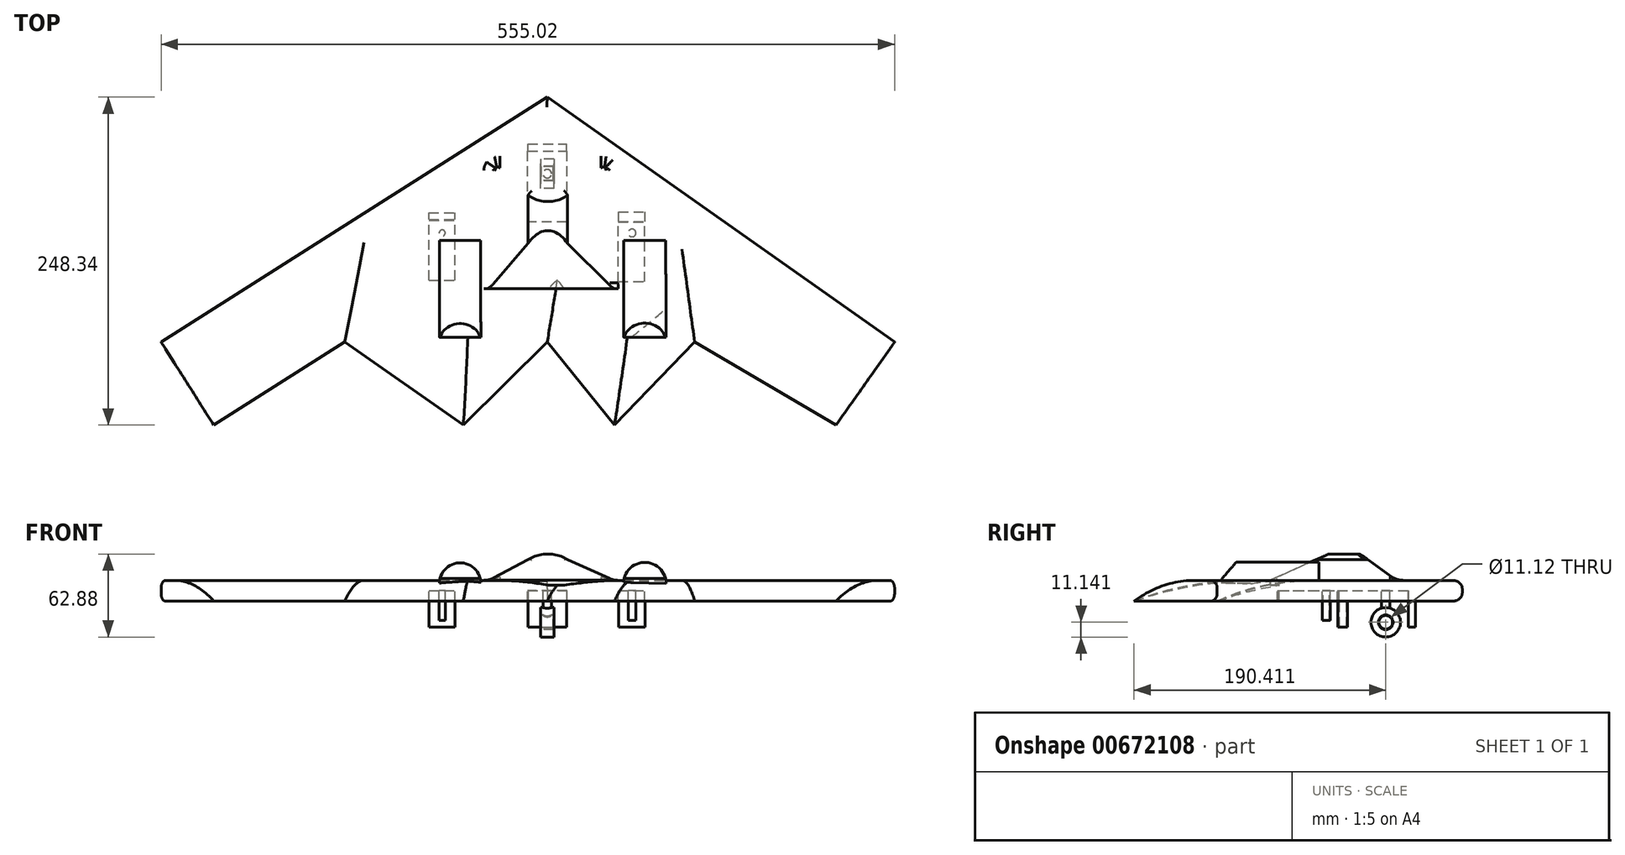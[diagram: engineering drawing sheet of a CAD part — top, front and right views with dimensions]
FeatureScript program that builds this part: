
annotation { "Feature Type Name" : "Feature", "Feature Type Description" : "" }
export const myFeature = defineFeature(function(context is Context, id is Id, definition is map)
    precondition{}
    {
        {
            var Q0;
            Q0=qCreatedBy(makeId("Top.planeOp"),FACE);
            var sketch = newSketch(context, id + "F0", { "sketchPlane" : qUnion([Q0])});
            skLineSegment(sketch, "E0", {"start": v(-292.15, -40.35) * mm, "end": v(0, 145.12) * mm});
            skLineSegment(sketch, "E1", {"start": v(0, 145.12) * mm, "end": v(262.87, -40.35) * mm});
            skLineSegment(sketch, "E2", {"start": v(262.87, -40.35) * mm, "end": v(218.51, -103.22) * mm});
            skLineSegment(sketch, "E3", {"start": v(-292.15, -40.35) * mm, "end": v(-252.24, -103.22) * mm});
            skLineSegment(sketch, "E4", {"start": v(-252.24, -103.22) * mm, "end": v(-153.22, -40.35) * mm});
            skLineSegment(sketch, "E5", {"start": v(-153.22, -40.35) * mm, "end": v(-63.45, -103.22) * mm});
            skLineSegment(sketch, "E6", {"start": v(218.51, -103.22) * mm, "end": v(111.56, -40.35) * mm});
            skLineSegment(sketch, "E7", {"start": v(111.56, -40.35) * mm, "end": v(50.9, -103.22) * mm});
            skLineSegment(sketch, "E8", {"start": v(50.9, -103.22) * mm, "end": v(0, -40.35) * mm});
            skLineSegment(sketch, "E9", {"start": v(0, -40.35) * mm, "end": v(-63.45, -103.22) * mm});
            skSolve(sketch);
        }
        {
            var Q0;
            Q0 = qSketchRegion(id + "F0", true);
            extrude(context, id + "F1", {"entities" : qUnion([Q0]), "endBound" : BoundingType.SYMMETRIC, "depth" : 15.75 * mm, "offsetDistance" : 25.4 * mm});
        }
        {
            var Q0;
            Q0=makeQuery(id+"F1.opExtrude","CAP_EDGE",EDGE,{"disambiguationData":[OSD([sQuery(id+"F0.wireOp",EDGE,"E1")])],"isStart":true});
            var Q1;
            Q1=makeQuery(id+"F1.opExtrude","CAP_EDGE",EDGE,{"disambiguationData":[OSD([sQuery(id+"F0.wireOp",EDGE,"E1")])],"isStart":false});
            var Q2;
            Q2=makeQuery(id+"F1.opExtrude","CAP_EDGE",EDGE,{"disambiguationData":[OSD([sQuery(id+"F0.wireOp",EDGE,"E0")])],"isStart":false});
            var Q3;
            Q3=makeQuery(id+"F1.opExtrude","CAP_EDGE",EDGE,{"disambiguationData":[OSD([sQuery(id+"F0.wireOp",EDGE,"E0")])],"isStart":true});
            fillet(context, id + "F2", {"entities" : qUnion([Q0, Q1, Q2, Q3]), "radius" : 6.13 * mm, "tangentPropagation" : true, "allowEdgeOverflow" : false});
        }
        {
            var Q0;
            Q0=makeQuery(id+"F1.opExtrude","CAP_EDGE",EDGE,{"disambiguationData":[OSD([sQuery(id+"F0.wireOp",EDGE,"E6")])],"isStart":false});
            var Q1;
            Q1=makeQuery(id+"F1.opExtrude","CAP_EDGE",EDGE,{"disambiguationData":[OSD([sQuery(id+"F0.wireOp",EDGE,"E7")])],"isStart":false});
            var Q2;
            Q2=makeQuery(id+"F1.opExtrude","CAP_EDGE",EDGE,{"disambiguationData":[OSD([sQuery(id+"F0.wireOp",EDGE,"E9")])],"isStart":false});
            var Q3;
            Q3=makeQuery(id+"F1.opExtrude","CAP_EDGE",EDGE,{"disambiguationData":[OSD([sQuery(id+"F0.wireOp",EDGE,"E4")])],"isStart":false});
            fillet(context, id + "F3", {"entities" : qUnion([Q0, Q1, Q2, Q3]), "radius" : 106.7 * mm, "tangentPropagation" : true, "allowEdgeOverflow" : false});
        }
        {
            var Q0;
            Q0=makeQuery(id+"F1.opExtrude","CAP_EDGE",EDGE,{"disambiguationData":[OSD([sQuery(id+"F0.wireOp",EDGE,"E5")])],"isStart":false});
            var Q1;
            Q1=makeQuery(id+"F1.opExtrude","CAP_EDGE",EDGE,{"disambiguationData":[OSD([sQuery(id+"F0.wireOp",EDGE,"E8")])],"isStart":false});
            fillet(context, id + "F4", {"entities" : qUnion([Q0, Q1]), "radius" : 163.11 * mm, "tangentPropagation" : true, "allowEdgeOverflow" : false});
        }
        {
            var Q0;
            Q0=qCreatedBy(makeId("Front.planeOp"),FACE);
            var sketch = newSketch(context, id + "F5", { "sketchPlane" : qUnion([Q0])});
            skArc(sketch, "E10", {"start": v(15.33, 23.56) * mm, "mid": v(0.48, 27.88) * mm, "end": v(-14.38, 23.56) * mm});
            skLineSegment(sketch, "E11", {"start": v(15.33, 23.56) * mm, "end": v(58.69, 4.08) * mm});
            skLineSegment(sketch, "E12", {"start": v(-14.38, 23.56) * mm, "end": v(-50.75, 4.4) * mm});
            skLineSegment(sketch, "E13", {"start": v(-50.75, 6.02) * mm, "end": v(-50.75, 4.4) * mm});
            skLineSegment(sketch, "E14", {"start": v(-50.75, 4.4) * mm, "end": v(58.69, 4.08) * mm});
            skSolve(sketch);
        }
        {
            var Q0;
            Q0 = qSketchRegion(id + "F5", true);
            extrude(context, id + "F6", {"entities" : qUnion([Q0]), "operationType" : NewBodyOperationType.ADD, "oppositeDirection" : true, "depth" : 94.74 * mm, "offsetDistance" : 25.4 * mm});
        }
        {
            var Q0;
            Q0=qCreatedBy(makeId("Right.planeOp"),FACE);
            var sketch = newSketch(context, id + "F7", { "sketchPlane" : qUnion([Q0])});
            skLineSegment(sketch, "E15", {"start": v(60.3, 33.11) * mm, "end": v(94.75, 8.43) * mm});
            skLineSegment(sketch, "E16", {"start": v(94.75, 8.43) * mm, "end": v(114.8, 41.67) * mm});
            skLineSegment(sketch, "E17", {"start": v(114.8, 41.67) * mm, "end": v(60.3, 33.11) * mm});
            skSolve(sketch);
        }
        {
            var Q0;
            Q0 = qSketchRegion(id + "F7", true);
            extrude(context, id + "F8", {"entities" : qUnion([Q0]), "operationType" : NewBodyOperationType.REMOVE, "endBound" : BoundingType.SYMMETRIC, "oppositeDirection" : true, "depth" : 1325.88 * mm, "offsetDistance" : 25.4 * mm});
        }
        {
            var Q0;
            Q0=makeQuery(id+"F8.boolean.opBoolean","INTERSECT",EDGE,{"derivedFrom":[makeQuery(id+"F6.opExtrude","CAP_FACE",FACE,{"disambiguationData":[OSD([sQuery(id+"F5.wireOp",EDGE,"E10"),sQuery(id+"F5.wireOp",EDGE,"E11"),sQuery(id+"F5.wireOp",EDGE,"E12"),sQuery(id+"F5.wireOp",EDGE,"E14")])],"isStart":false}),makeQuery(id+"F8.opExtrude","SWEPT_FACE",FACE,{"disambiguationData":[OSD([sQuery(id+"F7.wireOp",EDGE,"E15")])]})]});
            fillet(context, id + "F9", {"entities" : qUnion([Q0]), "radius" : 0.08 * mm, "tangentPropagation" : true, "allowEdgeOverflow" : false});
        }
        {
            var Q0;
            Q0=makeQuery(id+"F8.boolean.opBoolean","INTERSECT",EDGE,{"derivedFrom":[makeQuery(id+"F6.opExtrude","SWEPT_FACE",FACE,{"disambiguationData":[OSD([sQuery(id+"F5.wireOp",EDGE,"E11")])]}),makeQuery(id+"F8.opExtrude","SWEPT_FACE",FACE,{"disambiguationData":[OSD([sQuery(id+"F7.wireOp",EDGE,"E15")])]})]});
            var Q1;
            Q1=makeQuery(id+"F8.boolean.opBoolean","INTERSECT",EDGE,{"derivedFrom":[makeQuery(id+"F6.opExtrude","SWEPT_FACE",FACE,{"disambiguationData":[OSD([sQuery(id+"F5.wireOp",EDGE,"E10")])]}),makeQuery(id+"F8.opExtrude","SWEPT_FACE",FACE,{"disambiguationData":[OSD([sQuery(id+"F7.wireOp",EDGE,"E15")])]})]});
            var Q2;
            Q2=makeQuery(id+"F8.boolean.opBoolean","INTERSECT",EDGE,{"derivedFrom":[makeQuery(id+"F6.opExtrude","SWEPT_FACE",FACE,{"disambiguationData":[OSD([sQuery(id+"F5.wireOp",EDGE,"E12")])]}),makeQuery(id+"F8.opExtrude","SWEPT_FACE",FACE,{"disambiguationData":[OSD([sQuery(id+"F7.wireOp",EDGE,"E15")])]})]});
            fillet(context, id + "F10", {"entities" : qUnion([Q0, Q1, Q2]), "radius" : 5.08 * mm, "tangentPropagation" : true, "allowEdgeOverflow" : false});
        }
        {
            var Q0;
            Q0=qCreatedBy(makeId("Right.planeOp"),FACE);
            var sketch = newSketch(context, id + "F11", { "sketchPlane" : qUnion([Q0])});
            skLineSegment(sketch, "E18", {"start": v(0, 7.99) * mm, "end": v(46.44, 28.93) * mm});
            skLineSegment(sketch, "E19", {"start": v(46.44, 28.93) * mm, "end": v(-11.72, 36.75) * mm});
            skLineSegment(sketch, "E20", {"start": v(-11.72, 36.75) * mm, "end": v(0, 7.99) * mm});
            skSolve(sketch);
        }
        {
            var Q0;
            Q0 = qSketchRegion(id + "F11", true);
            extrude(context, id + "F12", {"entities" : qUnion([Q0]), "operationType" : NewBodyOperationType.REMOVE, "endBound" : BoundingType.SYMMETRIC, "oppositeDirection" : true, "depth" : 115.32 * mm, "offsetDistance" : 25.4 * mm});
        }
        {
            var Q0;
            Q0=qCreatedBy(makeId("Front.planeOp"),FACE);
            var sketch = newSketch(context, id + "F13", { "sketchPlane" : qUnion([Q0])});
            skArc(sketch, "E21", {"start": v(89.94, 5.45) * mm, "mid": v(74.32, 21.57) * mm, "end": v(57.8, 6.37) * mm});
            skArc(sketch, "E22", {"start": v(-50.13, 6.14) * mm, "mid": v(-66.32, 21.19) * mm, "end": v(-81.6, 5.22) * mm});
            skLineSegment(sketch, "E23", {"start": v(89.94, 5.45) * mm, "end": v(57.8, 6.37) * mm});
            skLineSegment(sketch, "E24", {"start": v(-50.13, 6.14) * mm, "end": v(-81.6, 5.22) * mm});
            skSolve(sketch);
        }
        {
            var Q0;
            Q0 = qSketchRegion(id + "F13", true);
            extrude(context, id + "F14", {"entities" : qUnion([Q0]), "operationType" : NewBodyOperationType.ADD, "endBound" : BoundingType.SYMMETRIC, "oppositeDirection" : true, "depth" : 73.15 * mm, "offsetDistance" : 25.4 * mm});
        }
        {
            var Q0;
            Q0=qCreatedBy(makeId("Right.planeOp"),FACE);
            var sketch = newSketch(context, id + "F15", { "sketchPlane" : qUnion([Q0])});
            skLineSegment(sketch, "E25", {"start": v(-36.97, 8.92) * mm, "end": v(-22.55, 25.54) * mm});
            skLineSegment(sketch, "E26", {"start": v(-22.55, 25.54) * mm, "end": v(-55.3, 20.9) * mm});
            skLineSegment(sketch, "E27", {"start": v(-55.3, 20.9) * mm, "end": v(-36.97, 8.92) * mm});
            skSolve(sketch);
        }
        {
            var Q0;
            Q0 = qSketchRegion(id + "F15", true);
            extrude(context, id + "F16", {"entities" : qUnion([Q0]), "operationType" : NewBodyOperationType.REMOVE, "endBound" : BoundingType.SYMMETRIC, "oppositeDirection" : true, "depth" : 313.94 * mm, "offsetDistance" : 25.4 * mm});
        }
        {
            var Q0;
            {var subQ0=makeQuery(id+"F6.opExtrude","CAP_FACE",FACE,{"disambiguationData":[OSD([sQuery(id+"F5.wireOp",EDGE,"E10"),sQuery(id+"F5.wireOp",EDGE,"E11"),sQuery(id+"F5.wireOp",EDGE,"E12"),sQuery(id+"F5.wireOp",EDGE,"E14")])],"isStart":false});Q0=makeQuery(id+"F9.opFillet","BLEND_EDGE",EDGE,{"blendedFrom":[makeQuery(id+"F8.boolean.opBoolean","INTERSECT",EDGE,{"derivedFrom":[subQ0,makeQuery(id+"F8.opExtrude","SWEPT_FACE",FACE,{"disambiguationData":[OSD([sQuery(id+"F7.wireOp",EDGE,"E15")])]})]}),subQ0],"blendedInto":[subQ0]});}
            var Q1;
            Q1=makeQuery(id+"F6.boolean.opBoolean","INTERSECT",EDGE,{"derivedFrom":[makeQuery(id+"F1.opExtrude","CAP_FACE",FACE,{"disambiguationData":[OSD([sQuery(id+"F0.wireOp",EDGE,"E0"),sQuery(id+"F0.wireOp",EDGE,"E1"),sQuery(id+"F0.wireOp",EDGE,"E2"),sQuery(id+"F0.wireOp",EDGE,"E3"),sQuery(id+"F0.wireOp",EDGE,"E4"),sQuery(id+"F0.wireOp",EDGE,"E5"),sQuery(id+"F0.wireOp",EDGE,"E6"),sQuery(id+"F0.wireOp",EDGE,"E7"),sQuery(id+"F0.wireOp",EDGE,"E8"),sQuery(id+"F0.wireOp",EDGE,"E9")])],"isStart":false}),makeQuery(id+"F6.opExtrude","CAP_FACE",FACE,{"disambiguationData":[OSD([sQuery(id+"F5.wireOp",EDGE,"E10"),sQuery(id+"F5.wireOp",EDGE,"E11"),sQuery(id+"F5.wireOp",EDGE,"E12"),sQuery(id+"F5.wireOp",EDGE,"E14")])],"isStart":false})]});
            fillet(context, id + "F17", {"entities" : qUnion([Q0, Q1]), "radius" : 15.33 * mm, "tangentPropagation" : true, "allowEdgeOverflow" : false});
        }
        {
            var Q0;
            Q0=qCreatedBy(makeId("Top.planeOp"),FACE);
            var sketch = newSketch(context, id + "F18", { "sketchPlane" : qUnion([Q0])});
            skLineSegment(sketch, "E28.bottom", {"start": v(14.85, 50.72) * mm, "end": v(-14.85, 50.72) * mm});
            skLineSegment(sketch, "E28.top", {"start": v(14.85, 104.24) * mm, "end": v(-14.85, 104.24) * mm});
            skLineSegment(sketch, "E28.left", {"start": v(14.85, 50.72) * mm, "end": v(14.85, 104.24) * mm});
            skLineSegment(sketch, "E28.right", {"start": v(-14.85, 50.72) * mm, "end": v(-14.85, 104.24) * mm});
            skPoint(sketch, "E28.middle", {"position": v(0, 77.48) * mm});
            skLineSegment(sketch, "E29.bottom", {"start": v(-89.47, 6.48) * mm, "end": v(-69.8, 6.48) * mm});
            skLineSegment(sketch, "E29.top", {"start": v(-89.47, 51.8) * mm, "end": v(-69.8, 51.8) * mm});
            skLineSegment(sketch, "E29.left", {"start": v(-89.47, 6.48) * mm, "end": v(-89.47, 51.8) * mm});
            skLineSegment(sketch, "E29.right", {"start": v(-69.8, 6.48) * mm, "end": v(-69.8, 51.8) * mm});
            skLineSegment(sketch, "E30.bottom", {"start": v(53.63, 5.38) * mm, "end": v(73.84, 5.38) * mm});
            skLineSegment(sketch, "E30.top", {"start": v(53.63, 50.72) * mm, "end": v(73.84, 50.72) * mm});
            skLineSegment(sketch, "E30.left", {"start": v(53.63, 5.38) * mm, "end": v(53.63, 50.72) * mm});
            skLineSegment(sketch, "E30.right", {"start": v(73.84, 5.38) * mm, "end": v(73.84, 50.72) * mm});
            skSolve(sketch);
        }
        {
            var Q0;
            Q0 = qSketchRegion(id + "F18", true);
            extrude(context, id + "F19", {"entities" : qUnion([Q0]), "operationType" : NewBodyOperationType.REMOVE, "oppositeDirection" : true, "depth" : 25.4 * mm, "offsetDistance" : 25.4 * mm});
        }
        {
            var Q0;
            Q0=qCreatedBy(makeId("Top.planeOp"),FACE);
            var sketch = newSketch(context, id + "F20", { "sketchPlane" : qUnion([Q0])});
            skLineSegment(sketch, "E31.bottom", {"start": v(-14.6, 104.17) * mm, "end": v(14.79, 104.17) * mm});
            skLineSegment(sketch, "E31.top", {"start": v(-14.6, 109.53) * mm, "end": v(14.79, 109.53) * mm});
            skLineSegment(sketch, "E31.left", {"start": v(-14.6, 104.17) * mm, "end": v(-14.6, 109.53) * mm});
            skLineSegment(sketch, "E31.right", {"start": v(14.79, 104.17) * mm, "end": v(14.79, 109.53) * mm});
            skLineSegment(sketch, "E32.bottom", {"start": v(53.92, 51.04) * mm, "end": v(74.06, 51.04) * mm});
            skLineSegment(sketch, "E32.top", {"start": v(53.92, 58.19) * mm, "end": v(74.06, 58.19) * mm});
            skLineSegment(sketch, "E32.left", {"start": v(53.92, 51.04) * mm, "end": v(53.92, 58.19) * mm});
            skLineSegment(sketch, "E32.right", {"start": v(74.06, 51.04) * mm, "end": v(74.06, 58.19) * mm});
            skLineSegment(sketch, "E33.bottom", {"start": v(-89.62, 52.34) * mm, "end": v(-69.81, 52.34) * mm});
            skLineSegment(sketch, "E33.top", {"start": v(-89.62, 57.54) * mm, "end": v(-69.81, 57.54) * mm});
            skLineSegment(sketch, "E33.left", {"start": v(-89.62, 52.34) * mm, "end": v(-89.62, 57.54) * mm});
            skLineSegment(sketch, "E33.right", {"start": v(-69.81, 52.34) * mm, "end": v(-69.81, 57.54) * mm});
            skSolve(sketch);
        }
        {
            var Q0;
            Q0 = qSketchRegion(id + "F20", true);
            extrude(context, id + "F21", {"entities" : qUnion([Q0]), "operationType" : NewBodyOperationType.ADD, "oppositeDirection" : true, "depth" : 27.43 * mm, "offsetDistance" : 25.4 * mm});
        }
        {
            var Q0;
            Q0=qCreatedBy(makeId("Top.planeOp"),FACE);
            var sketch = newSketch(context, id + "F22", { "sketchPlane" : qUnion([Q0])});
            skCircle(sketch, "E34", {"center": v(0, 87.15) * mm, "radius": 3.23 * mm});
            skSolve(sketch);
        }
        {
            var Q0;
            Q0 = qSketchRegion(id + "F22", true);
            extrude(context, id + "F23", {"entities" : qUnion([Q0]), "operationType" : NewBodyOperationType.ADD, "oppositeDirection" : true, "depth" : 20.83 * mm, "offsetDistance" : 25.4 * mm});
        }
        {
            var Q0;
            Q0=qCreatedBy(makeId("Right.planeOp"),FACE);
            var sketch = newSketch(context, id + "F24", { "sketchPlane" : qUnion([Q0])});
            skCircle(sketch, "E35", {"center": v(87.2, -23.86) * mm, "radius": 11.14 * mm});
            skCircle(sketch, "E36", {"center": v(87.2, -23.86) * mm, "radius": 5.56 * mm});
            skCircle(sketch, "E37", {"center": v(87.2, -23.86) * mm, "radius": 5.16 * mm});
            skSolve(sketch);
        }
        {
            var Q0;
            Q0 = qSketchRegion(id + "F24", true);
            extrude(context, id + "F25", {"entities" : qUnion([Q0]), "operationType" : NewBodyOperationType.ADD, "endBound" : BoundingType.SYMMETRIC, "depth" : 10.16 * mm, "offsetDistance" : 25.4 * mm});
        }
        {
            var Q0;
            Q0=makeQuery(id+"F24.imprint","IMPRINT",FACE,{"disambiguationData":[TD([[makeQuery(id+"F24.imprint","IMPRINT",EDGE,{"derivedFrom":sQuery(id+"F24.wireOp",EDGE,"E37")}),1.0]])]});
            extrude(context, id + "F26", {"entities" : qUnion([Q0]), "operationType" : NewBodyOperationType.ADD, "endBound" : BoundingType.SYMMETRIC, "depth" : 9.35 * mm, "offsetDistance" : 25.4 * mm});
        }
        {
            var Q0;
            Q0=qCreatedBy(makeId("Top.planeOp"),FACE);
            var sketch = newSketch(context, id + "F27", { "sketchPlane" : qUnion([Q0])});
            skCircle(sketch, "E38", {"center": v(-79.44, 42.24) * mm, "radius": 2.29 * mm});
            skCircle(sketch, "E39", {"center": v(64.2, 42.24) * mm, "radius": 2.93 * mm});
            skSolve(sketch);
        }
        {
            var Q0;
            Q0 = qSketchRegion(id + "F27", true);
            extrude(context, id + "F28", {"entities" : qUnion([Q0]), "operationType" : NewBodyOperationType.ADD, "oppositeDirection" : true, "depth" : 22.35 * mm, "offsetDistance" : 25.4 * mm});
        }
    });
